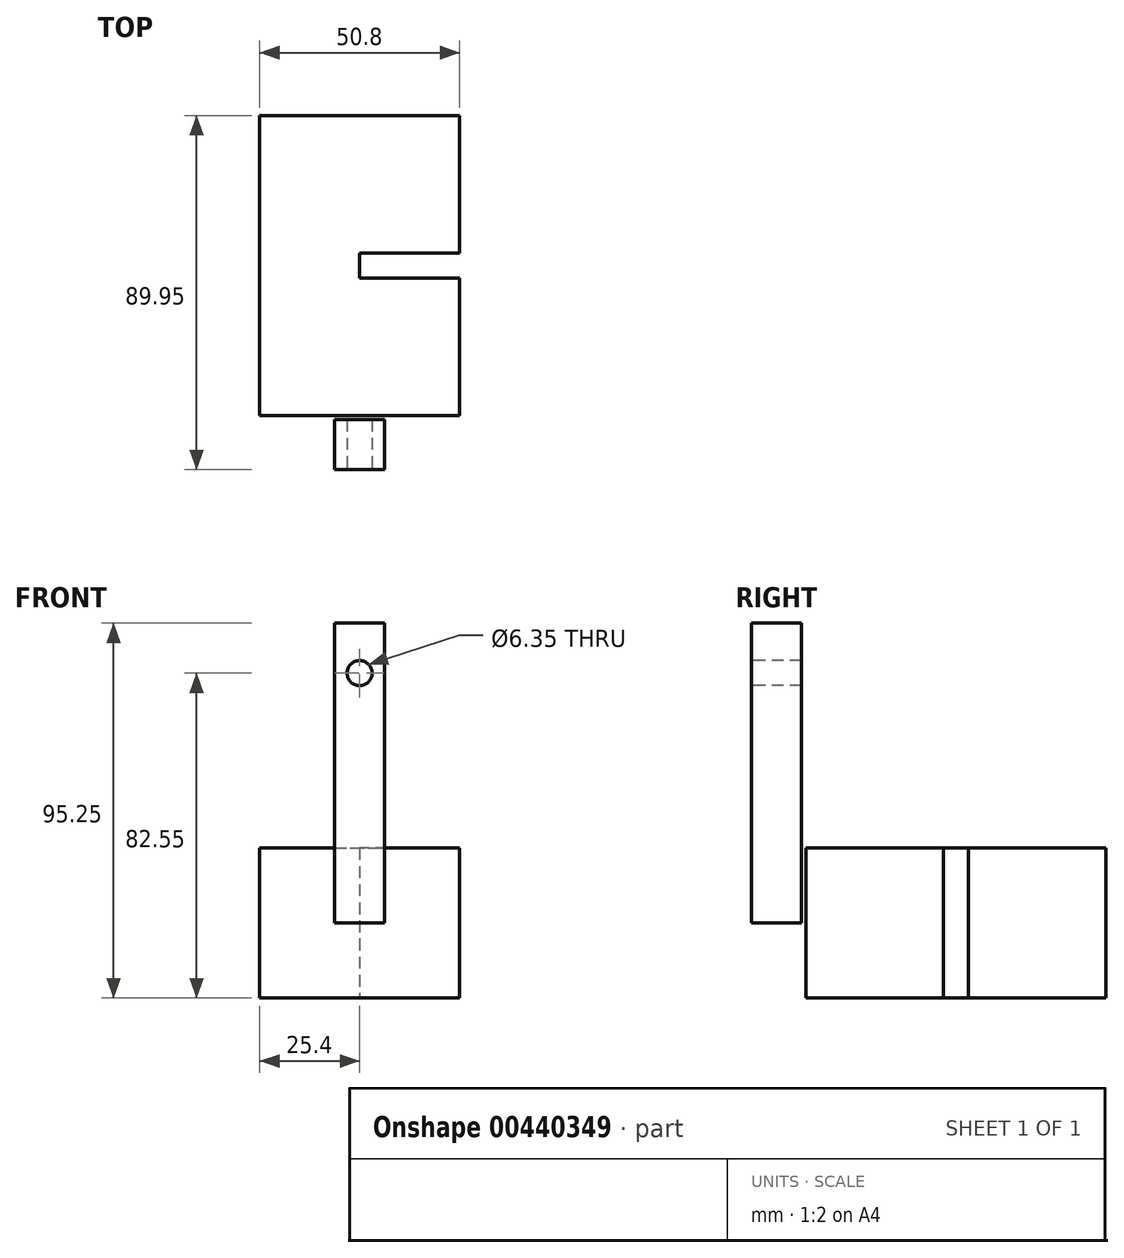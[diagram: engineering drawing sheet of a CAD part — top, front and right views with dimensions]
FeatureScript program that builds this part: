
annotation { "Feature Type Name" : "Feature", "Feature Type Description" : "" }
export const myFeature = defineFeature(function(context is Context, id is Id, definition is map)
    precondition{}
    {
        {
            var Q0;
            Q0=qCreatedBy(makeId("Top.planeOp"),FACE);
            var sketch = newSketch(context, id + "F0", { "sketchPlane" : qUnion([Q0])});
            skLineSegment(sketch, "E0.bottom", {"start": v(-25.4, 38.1) * mm, "end": v(25.4, 38.1) * mm});
            skLineSegment(sketch, "E0.top", {"start": v(-25.4, -38.1) * mm, "end": v(25.4, -38.1) * mm});
            skLineSegment(sketch, "E0.left", {"start": v(-25.4, 38.1) * mm, "end": v(-25.4, -38.1) * mm});
            skLineSegment(sketch, "E0.right", {"start": v(25.4, 38.1) * mm, "end": v(25.4, -38.1) * mm});
            skPoint(sketch, "E0.middle", {"position": v(0, 0) * mm});
            skLineSegment(sketch, "E1", {"start": v(0, 0) * mm, "end": v(25.4, 0) * mm});
            skLineSegment(sketch, "E2", {"start": v(25.4, 0) * mm, "end": v(25.4, 3.18) * mm});
            skLineSegment(sketch, "E3.bottom", {"start": v(25.4, 3.18) * mm, "end": v(0, 3.18) * mm});
            skLineSegment(sketch, "E3.top", {"start": v(25.4, -3.17) * mm, "end": v(0, -3.18) * mm});
            skLineSegment(sketch, "E3.left", {"start": v(25.4, 3.18) * mm, "end": v(25.4, -3.17) * mm});
            skLineSegment(sketch, "E3.right", {"start": v(0, 3.18) * mm, "end": v(0, -3.18) * mm});
            skSolve(sketch);
        }
        {
            var Q0;
            Q0=qCreatedBy(makeId("Top.planeOp"),FACE);
            var sketch = newSketch(context, id + "F1", { "sketchPlane" : qUnion([Q0])});
            skLineSegment(sketch, "E4", {"start": v(0, -39.15) * mm, "end": v(6.35, -39.15) * mm});
            skLineSegment(sketch, "E5.bottom", {"start": v(6.35, -39.15) * mm, "end": v(-6.35, -39.15) * mm});
            skLineSegment(sketch, "E5.top", {"start": v(6.35, -51.85) * mm, "end": v(-6.35, -51.85) * mm});
            skLineSegment(sketch, "E5.left", {"start": v(6.35, -39.15) * mm, "end": v(6.35, -51.85) * mm});
            skLineSegment(sketch, "E5.right", {"start": v(-6.35, -39.15) * mm, "end": v(-6.35, -51.85) * mm});
            skSolve(sketch);
        }
        {
            var Q0;
            {var subQ1=sQuery(id+"F0.wireOp",EDGE,"E0.bottom");Q0=makeQuery(id+"F0.imprint","IMPRINT",FACE,{"disambiguationData":[TD([[makeQuery(id+"F0.imprint","IMPRINT",EDGE,{"derivedFrom":subQ1}),-1.0]])]});}
            extrude(context, id + "F2", {"entities" : qUnion([Q0]), "endBound" : BoundingType.SYMMETRIC, "depth" : 38.1 * mm});
        }
        {
            var Q0;
            Q0=makeQuery(id+"F1.imprint","IMPRINT",FACE,{"disambiguationData":[TD([[makeQuery(id+"F1.imprint","IMPRINT",EDGE,{"derivedFrom":sQuery(id+"F1.wireOp",EDGE,"E5.top")}),-1.0]])]});
            extrude(context, id + "F3", {"entities" : qUnion([Q0]), "depth" : 76.2 * mm});
        }
        {
            var Q0;
            Q0=makeQuery(id+"F3.opExtrude","SWEPT_FACE",FACE,{"disambiguationData":[OSD([sQuery(id+"F1.wireOp",EDGE,"E5.top")])]});
            var sketch = newSketch(context, id + "F4", { "sketchPlane" : qUnion([Q0])});
            skLineSegment(sketch, "E6", {"start": v(0, 76.2) * mm, "end": v(0, 63.5) * mm});
            skPoint(sketch, "E6.endSnap0", {"position": v(0, 76.2) * mm});
            skCircle(sketch, "E7", {"center": v(0, 63.5) * mm, "radius": 3.18 * mm});
            skSolve(sketch);
        }
        {
            var Q0;
            Q0=makeQuery(id+"F4.imprint","IMPRINT",FACE,{"disambiguationData":[TD([[makeQuery(id+"F4.imprint","IMPRINT",EDGE,{"derivedFrom":sQuery(id+"F4.wireOp",EDGE,"E7")}),1.0]])]});
            extrude(context, id + "F5", {"entities" : qUnion([Q0]), "operationType" : NewBodyOperationType.REMOVE, "endBound" : BoundingType.SYMMETRIC, "oppositeDirection" : true, "depth" : 50.8 * mm});
        }
    });
